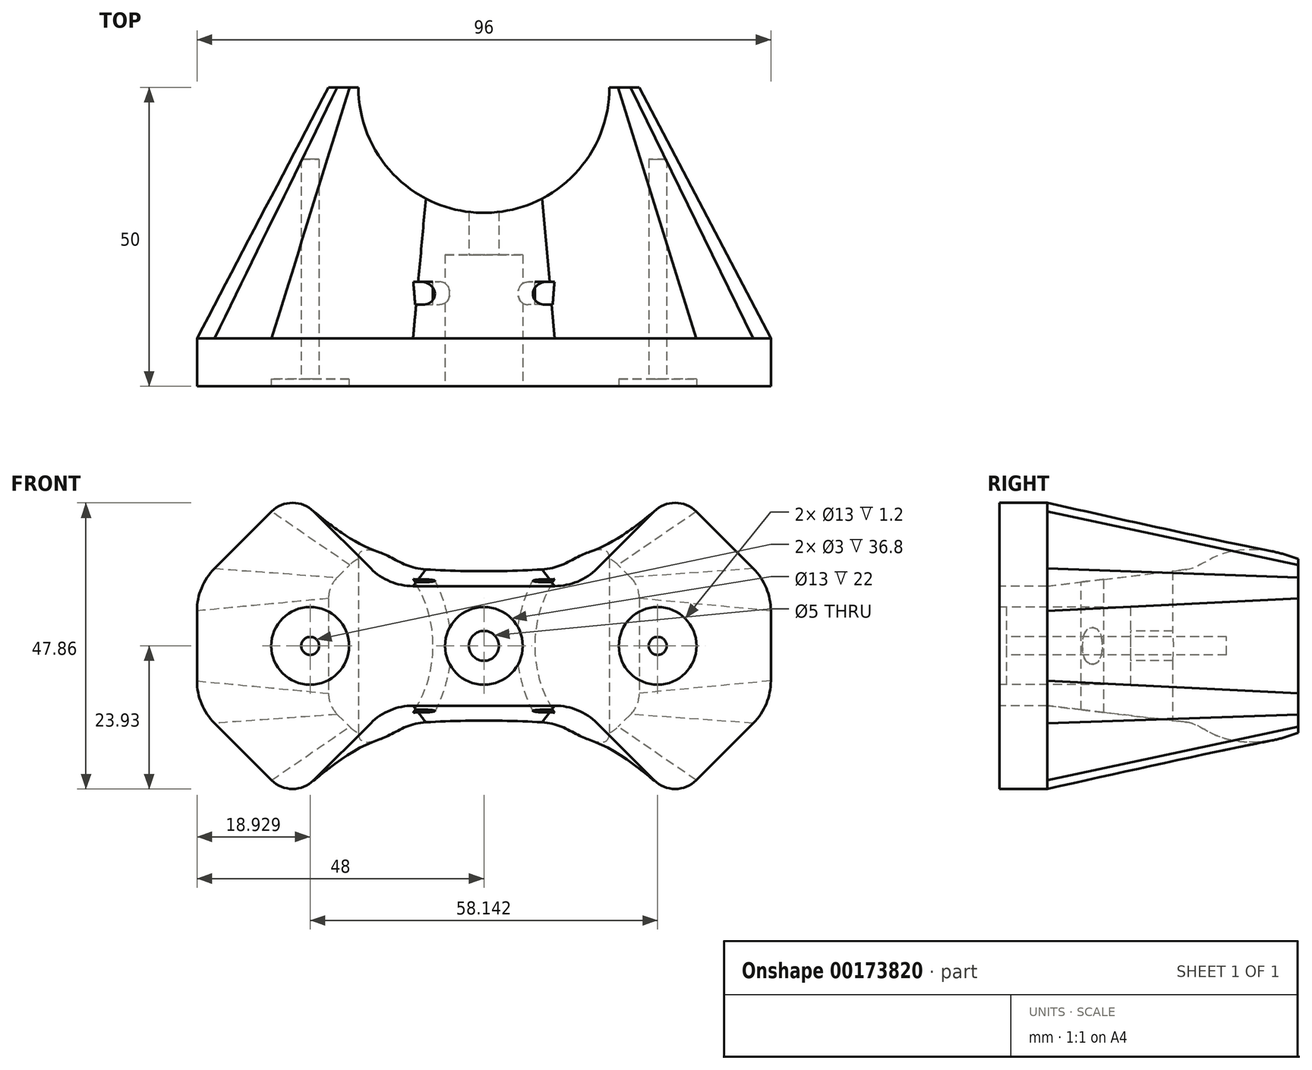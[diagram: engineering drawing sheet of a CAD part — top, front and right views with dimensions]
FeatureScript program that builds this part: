
annotation { "Feature Type Name" : "Feature", "Feature Type Description" : "" }
export const myFeature = defineFeature(function(context is Context, id is Id, definition is map)
    precondition{}
    {
        {
            var Q0;
            Q0=qCreatedBy(makeId("Front.planeOp"),FACE);
            var sketch = newSketch(context, id + "F0", { "sketchPlane" : qUnion([Q0])});
            skLineSegment(sketch, "E0", {"start": v(22, 90.61) * mm, "end": v(22, -125.4) * mm, "construction": true});
            skLineSegment(sketch, "E1", {"start": v(25.54, 3.54) * mm, "end": v(146.18, 124.18) * mm, "construction": true});
            skLineSegment(sketch, "E2", {"start": v(25.54, -3.54) * mm, "end": v(137.79, -115.79) * mm, "construction": true});
            skPoint(sketch, "E3.visualSharp", {"position": v(22, 0) * mm});
            skArc(sketch, "E3.filletArc", {"start": v(25.54, 3.54) * mm, "mid": v(24.07, 0) * mm, "end": v(25.54, -3.54) * mm, "construction": true});
            skLineSegment(sketch, "E4.0", {"start": v(24.2, 4.88) * mm, "end": v(144.83, 125.52) * mm});
            skArc(sketch, "E4.1", {"start": v(24.2, 4.88) * mm, "mid": v(22.17, 0) * mm, "end": v(24.2, -4.88) * mm});
            skLineSegment(sketch, "E4.2", {"start": v(24.2, -4.88) * mm, "end": v(136.44, -117.13) * mm});
            skLineSegment(sketch, "E5.0", {"start": v(26.88, 2.2) * mm, "end": v(147.52, 122.83) * mm});
            skArc(sketch, "E5.1", {"start": v(26.88, 2.2) * mm, "mid": v(25.97, 0) * mm, "end": v(26.88, -2.2) * mm});
            skLineSegment(sketch, "E5.2", {"start": v(26.88, -2.2) * mm, "end": v(139.13, -114.44) * mm});
            skLineSegment(sketch, "E6", {"start": v(0, 0) * mm, "end": v(0, 10) * mm});
            skLineSegment(sketch, "E7", {"start": v(0, 10) * mm, "end": v(11.86, 10) * mm});
            skLineSegment(sketch, "E8", {"start": v(48, 5.86) * mm, "end": v(48, -5.86) * mm});
            skLineSegment(sketch, "E9", {"start": v(0, -10) * mm, "end": v(0, 0) * mm});
            skLineSegment(sketch, "E10", {"start": v(45.07, 12.93) * mm, "end": v(35.54, 22.46) * mm});
            skLineSegment(sketch, "E11", {"start": v(28.46, 22.46) * mm, "end": v(18.93, 12.93) * mm});
            skLineSegment(sketch, "E12", {"start": v(18.93, -12.93) * mm, "end": v(28.46, -22.46) * mm});
            skLineSegment(sketch, "E13", {"start": v(35.54, -22.46) * mm, "end": v(45.07, -12.93) * mm});
            skLineSegment(sketch, "E14.trimOffspring", {"start": v(11.86, -10) * mm, "end": v(0, -10) * mm});
            skCircle(sketch, "E15", {"center": v(29.07, 0) * mm, "radius": 6.5 * mm});
            skPoint(sketch, "E16.visualSharp", {"position": v(16, 10) * mm});
            skArc(sketch, "E16.filletArc", {"start": v(11.86, 10) * mm, "mid": v(15.68, 10.76) * mm, "end": v(18.93, 12.93) * mm});
            skPoint(sketch, "E17.visualSharp", {"position": v(16, -10) * mm});
            skArc(sketch, "E17.filletArc", {"start": v(18.93, -12.93) * mm, "mid": v(15.68, -10.76) * mm, "end": v(11.86, -10) * mm});
            skPoint(sketch, "E18.visualSharp", {"position": v(32, 26) * mm});
            skArc(sketch, "E18.filletArc", {"start": v(35.54, 22.46) * mm, "mid": v(32, 23.93) * mm, "end": v(28.46, 22.46) * mm});
            skPoint(sketch, "E19.visualSharp", {"position": v(32, -26) * mm});
            skArc(sketch, "E19.filletArc", {"start": v(28.46, -22.46) * mm, "mid": v(32, -23.93) * mm, "end": v(35.54, -22.46) * mm});
            skPoint(sketch, "E20.visualSharp", {"position": v(48, 10) * mm});
            skArc(sketch, "E20.filletArc", {"start": v(48, 5.86) * mm, "mid": v(47.24, 9.68) * mm, "end": v(45.07, 12.93) * mm});
            skPoint(sketch, "E21.visualSharp", {"position": v(48, -10) * mm});
            skArc(sketch, "E21.filletArc", {"start": v(45.07, -12.93) * mm, "mid": v(47.24, -9.68) * mm, "end": v(48, -5.86) * mm});
            skSolve(sketch);
        }
        {
            var Q0;
            Q0=qCreatedBy(makeId("Top.planeOp"),FACE);
            var sketch = newSketch(context, id + "F1", { "sketchPlane" : qUnion([Q0])});
            skLineSegment(sketch, "E22", {"start": v(-181.89, 100) * mm, "end": v(201.11, 100) * mm, "construction": true});
            skArc(sketch, "E23", {"start": v(0, 29) * mm, "mid": v(21, 50) * mm, "end": v(0, 71) * mm});
            skLineSegment(sketch, "E24", {"start": v(24, 0) * mm, "end": v(24, 0) * mm});
            skLineSegment(sketch, "E25", {"start": v(0, 29) * mm, "end": v(0, 71) * mm});
            skSolve(sketch);
        }
        {
            var Q0;
            Q0 = qSketchRegion(id + "F0", true);
            var Q1;
            {var subQ0=sQuery(id+"F0.wireOp",EDGE,"E5.1");Q1=makeQuery(id+"F0.imprint","IMPRINT",FACE,{"disambiguationData":[TD([[makeQuery(id+"F0.imprint","IMPRINT",EDGE,{"derivedFrom":subQ0}),1.0]])]});}
            var Q2;
            {var subQ0=sQuery(id+"F0.wireOp",EDGE,"E5.1");Q2=makeQuery(id+"F0.imprint","IMPRINT",FACE,{"disambiguationData":[TD([[makeQuery(id+"F0.imprint","IMPRINT",EDGE,{"derivedFrom":subQ0}),-1.0]])]});}
            extrude(context, id + "F2", {"entities" : qUnion([Q0, Q1, Q2]), "oppositeDirection" : true, "depth" : 8 * mm, "offsetDistance" : 25 * mm});
        }
        {
            var Q0;
            Q0=qCreatedBy(makeId("Front.planeOp"),FACE);
            cPlane(context, id + "F3", {"entities" : qUnion([Q0]), "cplaneType" : CPlaneType.OFFSET, "offset" : 50 * mm, "oppositeDirection" : true, "width" : 150 * mm, "height" : 150 * mm});
        }
        {
            var Q0;
            Q0=qCreatedBy(id+"F3.planeOp",FACE);
            var sketch = newSketch(context, id + "F4", { "sketchPlane" : qUnion([Q0])});
            skLineSegment(sketch, "E26.bottom", {"start": v(18.93, 15) * mm, "end": v(12, 15) * mm});
            skLineSegment(sketch, "E26.top", {"start": v(18.93, -15) * mm, "end": v(12, -15) * mm});
            skLineSegment(sketch, "E26.left", {"start": v(26, 7.93) * mm, "end": v(26, -7.93) * mm});
            skLineSegment(sketch, "E26.right", {"start": v(0, 15) * mm, "end": v(0, -15) * mm});
            skLineSegment(sketch, "E27", {"start": v(8, 15) * mm, "end": v(0, 15) * mm});
            skLineSegment(sketch, "E28", {"start": v(12, 15) * mm, "end": v(8, 15) * mm});
            skLineSegment(sketch, "E29", {"start": v(24.54, 11.46) * mm, "end": v(22.46, 13.54) * mm});
            skLineSegment(sketch, "E30", {"start": v(24.54, -11.46) * mm, "end": v(22.46, -13.54) * mm});
            skPoint(sketch, "E31.visualSharp", {"position": v(21, 15) * mm});
            skArc(sketch, "E31.filletArc", {"start": v(22.46, 13.54) * mm, "mid": v(20.84, 14.62) * mm, "end": v(18.93, 15) * mm});
            skPoint(sketch, "E32.visualSharp", {"position": v(21, -15) * mm});
            skArc(sketch, "E32.filletArc", {"start": v(18.93, -15) * mm, "mid": v(20.84, -14.62) * mm, "end": v(22.46, -13.54) * mm});
            skPoint(sketch, "E33.visualSharp", {"position": v(26, -10) * mm});
            skArc(sketch, "E33.filletArc", {"start": v(24.54, -11.46) * mm, "mid": v(25.62, -9.84) * mm, "end": v(26, -7.93) * mm});
            skPoint(sketch, "E34.visualSharp", {"position": v(26, 10) * mm});
            skArc(sketch, "E34.filletArc", {"start": v(26, 7.93) * mm, "mid": v(25.62, 9.84) * mm, "end": v(24.54, 11.46) * mm});
            skLineSegment(sketch, "E35", {"start": v(8, -15) * mm, "end": v(0, -15) * mm});
            skLineSegment(sketch, "E36", {"start": v(12, -15) * mm, "end": v(8, -15) * mm});
            skSolve(sketch);
        }
        {
            var Q0;
            Q0=makeQuery(id+"F2.opExtrude","CAP_FACE",FACE,{"disambiguationData":[OSD([sQuery(id+"F0.wireOp",EDGE,"E6"),sQuery(id+"F0.wireOp",EDGE,"E7"),sQuery(id+"F0.wireOp",EDGE,"E8"),sQuery(id+"F0.wireOp",EDGE,"E9"),sQuery(id+"F0.wireOp",EDGE,"E10"),sQuery(id+"F0.wireOp",EDGE,"E11"),sQuery(id+"F0.wireOp",EDGE,"E12"),sQuery(id+"F0.wireOp",EDGE,"E13"),sQuery(id+"F0.wireOp",EDGE,"E14.trimOffspring"),sQuery(id+"F0.wireOp",EDGE,"E15"),sQuery(id+"F0.wireOp",EDGE,"E16.filletArc"),sQuery(id+"F0.wireOp",EDGE,"E17.filletArc"),sQuery(id+"F0.wireOp",EDGE,"E18.filletArc"),sQuery(id+"F0.wireOp",EDGE,"E19.filletArc"),sQuery(id+"F0.wireOp",EDGE,"E20.filletArc"),sQuery(id+"F0.wireOp",EDGE,"E21.filletArc")])],"isStart":false});
            var Q1;
            Q1 = qSketchRegion(id + "F4", true);
            loft(context, id + "F5", {"sheetProfilesArray" : [{ "sheetProfileEntities" : qUnion([Q0]) }, { "sheetProfileEntities" : qUnion([Q1]) }]});
        }
        {
            var Q0;
            Q0 = qSketchRegion(id + "F1", true);
            extrude(context, id + "F6", {"entities" : qUnion([Q0]), "operationType" : NewBodyOperationType.REMOVE, "depth" : 34.6 * mm, "offsetDistance" : 25 * mm, "symmetric" : true});
        }
        {
            var Q0;
            Q0=makeQuery(id+"F2.opExtrude","SWEPT_FACE",FACE,{"disambiguationData":[OSD([sQuery(id+"F0.wireOp",EDGE,"E10")])]});
            var sketch = newSketch(context, id + "F7", { "sketchPlane" : qUnion([Q0])});
            skPoint(sketch, "E37.0", {"position": v(13.66, 0) * mm});
            skPoint(sketch, "E38.0", {"position": v(17.46, 0) * mm});
            skLineSegment(sketch, "E39", {"start": v(17.46, 0) * mm, "end": v(17.46, 1.1) * mm});
            skArc(sketch, "E40", {"start": v(17.46, 1.1) * mm, "mid": v(15.56, 3) * mm, "end": v(13.66, 1.1) * mm});
            skLineSegment(sketch, "E41", {"start": v(17.46, 0) * mm, "end": v(13.66, 0) * mm});
            skLineSegment(sketch, "E42", {"start": v(13.66, 0) * mm, "end": v(13.66, 1.1) * mm});
            skSolve(sketch);
        }
        {
            var Q0;
            Q0=makeQuery(id+"F7.imprint","IMPRINT",FACE,{"disambiguationData":[TD([[makeQuery(id+"F7.imprint","IMPRINT",EDGE,{"derivedFrom":sQuery(id+"F7.wireOp",EDGE,"E39")}),1.0]])]});
            var Q1;
            Q1=sQuery(id+"F0.wireOp",EDGE,"E4.0");
            var Q2;
            Q2=sQuery(id+"F0.wireOp",EDGE,"E4.1");
            var Q3;
            Q3=sQuery(id+"F0.wireOp",EDGE,"E4.2");
            sweep(context, id + "F8", {"operationType" : NewBodyOperationType.REMOVE, "profiles" : qUnion([Q0]), "path" : qUnion([Q1, Q2, Q3])});
        }
        {
            var Q0;
            {var subQ0=sQuery(id+"F0.wireOp",EDGE,"E5.1");Q0=makeQuery(id+"F0.imprint","IMPRINT",FACE,{"disambiguationData":[TD([[makeQuery(id+"F0.imprint","IMPRINT",EDGE,{"derivedFrom":subQ0}),1.0]])]});}
            var sketch = newSketch(context, id + "F9", { "sketchPlane" : qUnion([Q0])});
            skCircle(sketch, "E43.0", {"center": v(29.07, 0) * mm, "radius": 6.5 * mm});
            skSolve(sketch);
        }
        {
            var Q0;
            Q0 = qSketchRegion(id + "F9", true);
            extrude(context, id + "F10", {"entities" : qUnion([Q0]), "operationType" : NewBodyOperationType.REMOVE, "oppositeDirection" : true, "depth" : 1.2 * mm, "offsetDistance" : 25 * mm});
        }
        {
            var Q0;
            {var subQ0=sQuery(id+"F0.wireOp",EDGE,"E5.1");Q0=makeQuery(id+"F0.imprint","IMPRINT",FACE,{"disambiguationData":[TD([[makeQuery(id+"F0.imprint","IMPRINT",EDGE,{"derivedFrom":subQ0}),1.0]])]});}
            var sketch = newSketch(context, id + "F11", { "sketchPlane" : qUnion([Q0])});
            skPoint(sketch, "E44.0", {"position": v(29.07, 0) * mm});
            skCircle(sketch, "E45", {"center": v(29.07, 0) * mm, "radius": 1.5 * mm});
            skSolve(sketch);
        }
        {
            var Q0;
            Q0 = qSketchRegion(id + "F11", true);
            extrude(context, id + "F12", {"entities" : qUnion([Q0]), "operationType" : NewBodyOperationType.REMOVE, "oppositeDirection" : true, "depth" : 38 * mm, "offsetDistance" : 25 * mm});
        }
        {
            var Q0;
            Q0=makeQuery(id+"F5.opLoft","SWEPT_BODY",BODY,{"disambiguationData":[OSD([sQuery(id+"F0.wireOp",EDGE,"E6"),sQuery(id+"F0.wireOp",EDGE,"E7"),sQuery(id+"F0.wireOp",EDGE,"E8"),sQuery(id+"F0.wireOp",EDGE,"E9"),sQuery(id+"F0.wireOp",EDGE,"E10"),sQuery(id+"F0.wireOp",EDGE,"E11"),sQuery(id+"F0.wireOp",EDGE,"E12"),sQuery(id+"F0.wireOp",EDGE,"E13"),sQuery(id+"F0.wireOp",EDGE,"E14.trimOffspring"),sQuery(id+"F0.wireOp",EDGE,"E16.filletArc"),sQuery(id+"F0.wireOp",EDGE,"E17.filletArc"),sQuery(id+"F0.wireOp",EDGE,"E18.filletArc"),sQuery(id+"F0.wireOp",EDGE,"E19.filletArc"),sQuery(id+"F0.wireOp",EDGE,"E20.filletArc"),sQuery(id+"F0.wireOp",EDGE,"E21.filletArc"),makeQuery(id+"F4.imprint","IMPRINT",FACE,{"disambiguationData":[TD([[makeQuery(id+"F4.imprint","IMPRINT",EDGE,{"derivedFrom":sQuery(id+"F4.wireOp",EDGE,"E26.bottom")}),1.0]])]})])]});
            var Q1;
            Q1=makeQuery(id+"F2.opExtrude","SWEPT_BODY",BODY,{"disambiguationData":[OSD([sQuery(id+"F0.wireOp",EDGE,"E6"),sQuery(id+"F0.wireOp",EDGE,"E7"),sQuery(id+"F0.wireOp",EDGE,"E8"),sQuery(id+"F0.wireOp",EDGE,"E9"),sQuery(id+"F0.wireOp",EDGE,"E10"),sQuery(id+"F0.wireOp",EDGE,"E11"),sQuery(id+"F0.wireOp",EDGE,"E12"),sQuery(id+"F0.wireOp",EDGE,"E13"),sQuery(id+"F0.wireOp",EDGE,"E14.trimOffspring"),sQuery(id+"F0.wireOp",EDGE,"E16.filletArc"),sQuery(id+"F0.wireOp",EDGE,"E17.filletArc"),sQuery(id+"F0.wireOp",EDGE,"E18.filletArc"),sQuery(id+"F0.wireOp",EDGE,"E19.filletArc"),sQuery(id+"F0.wireOp",EDGE,"E20.filletArc"),sQuery(id+"F0.wireOp",EDGE,"E21.filletArc")])]});
            var Q2;
            Q2=qCreatedBy(makeId("Right.planeOp"),FACE);
            mirror(context, id + "F13", {"operationType" : NewBodyOperationType.ADD, "entities" : qUnion([Q0, Q1]), "mirrorPlane" : qUnion([Q2])});
        }
        {
            var Q0;
            {var subQ0=sQuery(id+"F0.wireOp",EDGE,"E18.filletArc");var subQ1=sQuery(id+"F0.wireOp",EDGE,"E17.filletArc");var subQ2=sQuery(id+"F0.wireOp",EDGE,"E16.filletArc");var subQ3=sQuery(id+"F0.wireOp",EDGE,"E14.trimOffspring");var subQ4=sQuery(id+"F0.wireOp",EDGE,"E13");var subQ5=sQuery(id+"F0.wireOp",EDGE,"E12");var subQ6=sQuery(id+"F0.wireOp",EDGE,"E9");var subQ7=sQuery(id+"F0.wireOp",EDGE,"E6");var subQ8=sQuery(id+"F0.wireOp",EDGE,"E7");var subQ9=sQuery(id+"F0.wireOp",EDGE,"E10");var subQ10=sQuery(id+"F0.wireOp",EDGE,"E11");var subQ11=sQuery(id+"F0.wireOp",EDGE,"E19.filletArc");var subQ13=makeQuery(id+"F8.boolean.opBoolean","SPLIT",FACE,{"disambiguationData":[TD([makeQuery(id+"F2.opExtrude","SWEPT_FACE",FACE,{"disambiguationData":[OSD([subQ8])]})])],"derivedFrom":makeQuery(id+"F2.opExtrude","CAP_FACE",FACE,{"disambiguationData":[OSD([subQ7,subQ8,sQuery(id+"F0.wireOp",EDGE,"E8"),subQ6,subQ9,subQ10,subQ5,subQ4,subQ3,subQ2,subQ1,subQ0,subQ11,sQuery(id+"F0.wireOp",EDGE,"E20.filletArc"),sQuery(id+"F0.wireOp",EDGE,"E21.filletArc")])],"isStart":true})});Q0=makeQuery(id+"F13.boolean.opBoolean","MERGE",FACE,{"derivedFrom":[subQ13,makeQuery(id+"F13.opPattern","COPY",FACE,{"derivedFrom":subQ13,"instanceName":"1"})]});}
            var sketch = newSketch(context, id + "F14", { "sketchPlane" : qUnion([Q0])});
            skCircle(sketch, "E46", {"center": v(0, 0) * mm, "radius": 6.5 * mm});
            skSolve(sketch);
        }
        {
            var Q0;
            Q0 = qSketchRegion(id + "F14", true);
            extrude(context, id + "F15", {"entities" : qUnion([Q0]), "operationType" : NewBodyOperationType.REMOVE, "oppositeDirection" : true, "depth" : 22 * mm, "offsetDistance" : 25 * mm});
        }
        {
            var Q0;
            {var subQ8=sQuery(id+"F0.wireOp",EDGE,"E4.1");Q0=makeQuery(id+"F0.imprint","IMPRINT",FACE,{"disambiguationData":[TD([[makeQuery(id+"F0.imprint","IMPRINT",EDGE,{"derivedFrom":subQ8}),-1.0]])]});}
            var sketch = newSketch(context, id + "F16", { "sketchPlane" : qUnion([Q0])});
            skCircle(sketch, "E47", {"center": v(0, 0) * mm, "radius": 2.5 * mm});
            skSolve(sketch);
        }
        {
            var Q0;
            Q0 = qSketchRegion(id + "F16", true);
            extrude(context, id + "F17", {"entities" : qUnion([Q0]), "operationType" : NewBodyOperationType.REMOVE, "endBound" : BoundingType.THROUGH_ALL, "oppositeDirection" : true, "depth" : 25 * mm, "offsetDistance" : 25 * mm});
        }
    });
